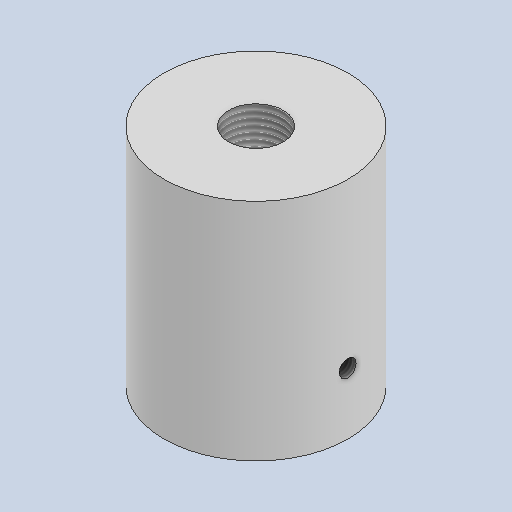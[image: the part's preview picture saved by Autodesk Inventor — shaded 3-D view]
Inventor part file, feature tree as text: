
AUTODESK INVENTOR PART (.ipt)
format: ipt  version: 2023 (Build 270158000, 158)  size: 228,864 bytes
history: native  units: mm
features: sketch x5, other x2, extrude x2, hole x2
ambient origin geometry x8: Origin, YZ Plane, XZ Plane, XY Plane, X Axis, Y Axis, Z Axis, Center Point
bodies: Body1 (feature_tree)
feature tree (11):
  other  "Твердое тело1"
  extrude  "Выдавливание1"  Depth=45.0mm
  sketch  "Эскиз2"
  other  "РабПлоскость1"
  hole  "Отверстие1"  [1 undecoded]
  hole  "Отверстие2"  [1 undecoded]
  extrude  "Выдавливание2"  Depth=5.0mm
  sketch  "Эскиз1"
  sketch  "Эскиз3"
  sketch  "Эскиз4"
  sketch  "Эскиз5"
note: 2 required parameter values undecoded (feature->parameter linkage not recoverable at this tier; creation-order binding heuristic only, values carry confidence <= 0.55)
